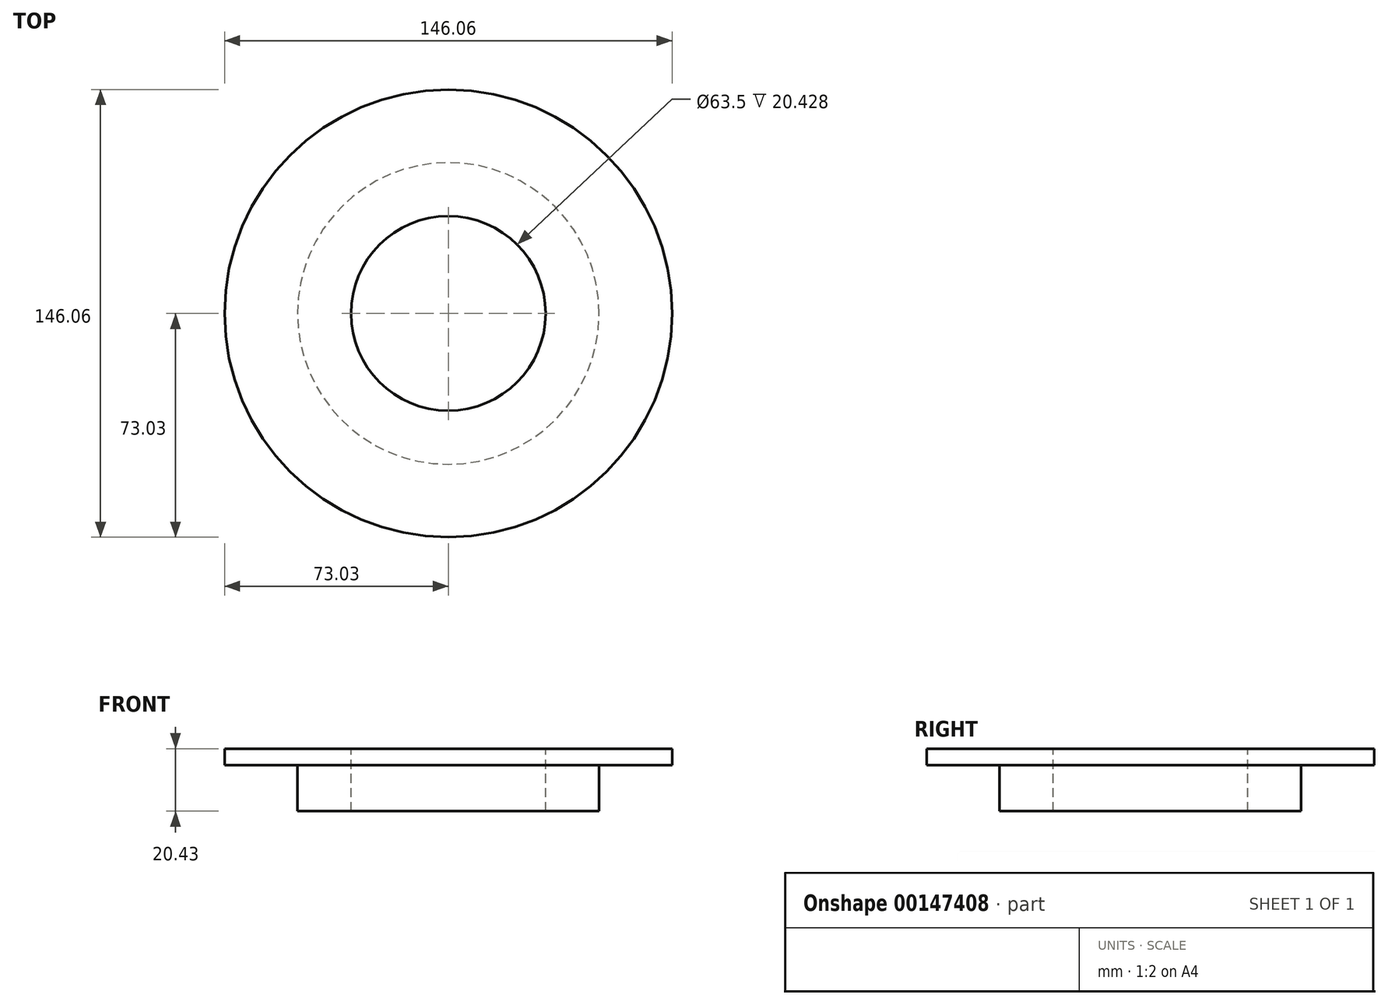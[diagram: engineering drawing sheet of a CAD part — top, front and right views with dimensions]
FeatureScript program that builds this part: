
annotation { "Feature Type Name" : "Feature", "Feature Type Description" : "" }
export const myFeature = defineFeature(function(context is Context, id is Id, definition is map)
    precondition{}
    {
        {
            var Q0;
            Q0=qCreatedBy(makeId("Front.planeOp"),FACE);
            var sketch = newSketch(context, id + "F0", { "sketchPlane" : qUnion([Q0])});
            skLineSegment(sketch, "E0", {"start": v(-73.03, 7.73) * mm, "end": v(-73.03, 2.38) * mm});
            skLineSegment(sketch, "E1", {"start": v(-73.03, 2.38) * mm, "end": v(-49.21, 2.38) * mm});
            skLineSegment(sketch, "E2", {"start": v(-49.21, 2.38) * mm, "end": v(-49.21, -12.7) * mm});
            skLineSegment(sketch, "E3", {"start": v(-49.21, -12.7) * mm, "end": v(-31.75, -12.7) * mm});
            skLineSegment(sketch, "E4", {"start": v(-31.75, -12.7) * mm, "end": v(-31.75, 7.73) * mm});
            skLineSegment(sketch, "E5", {"start": v(-31.75, 7.73) * mm, "end": v(-73.03, 7.73) * mm});
            skLineSegment(sketch, "E6", {"start": v(0, 15.7) * mm, "end": v(0, -21.54) * mm, "construction": true});
            skSolve(sketch);
        }
        {
            var Q0;
            Q0 = qSketchRegion(id + "F0", true);
            var Q1;
            Q1=sQuery(id+"F0.wireOp",EDGE,"E6");
            revolve(context, id + "F1", {"entities" : qUnion([Q0]), "axis" : qUnion([Q1]), "revolveType" : RevolveType.FULL});
        }
    });
